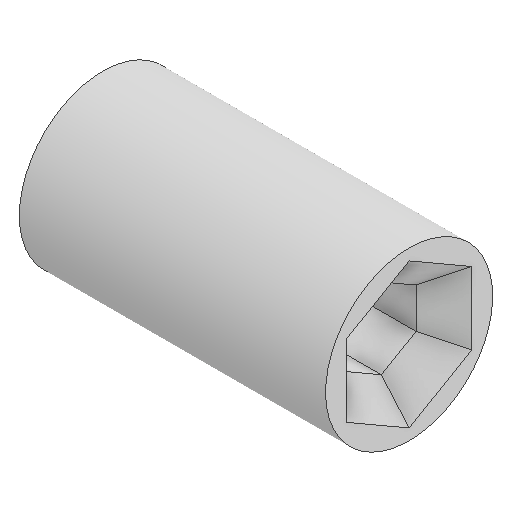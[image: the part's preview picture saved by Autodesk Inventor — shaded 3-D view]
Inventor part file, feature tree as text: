
AUTODESK INVENTOR PART (.ipt)
format: ipt  version: 2024.1 (Build 281209000, 209)  size: 125,952 bytes
history: native  units: mm
features: extrude x2, sketch x2, chamfer x1, projected_geometry x1
ambient origin geometry x8: Origin, YZ Plane, XZ Plane, XY Plane, X Axis, Y Axis, Z Axis, Center Point
bodies: Volumenkörper1 (feature_tree)
feature tree (6):
  extrude  "Extrusion1"  Depth=2.5mm
  extrude  "Extrusion2"  Depth=5.0mm TaperAngle=0.0deg
  chamfer  "Fase1"  Distance=1.0mm Angle=45.0deg
  sketch  "Skizze1"  dims[d0=6.0mm d1=2.5mm]
  sketch  "Skizze2"  dims[d2=6.0mm d3=0.0mm d4=5.0mm d5=0.0mm d7=1.0mm d8=2.0mm d9=45.0deg]
  projected_geometry  "Projizierte Kontur1"
